# Revit family: Gira_104000
name_source: partatom
category: Elektroinstallationen
revit_build: Autodesk Revit 2017 (Build: 20160225_1515(x64)
units: mm (PartAtom-declared; Revit-internal decimal feet)

## family parameters
Basisbauteil = Fläche
Beim Laden mit Abzugskörper schneiden = Nein
Bemaßung runder Anschluss = Durchmesser verwenden
Beschriftungsausrichtung beibehalten = Nein
Gemeinsam genutzt = Nein
Raumberechnungspunkt = Nein
Teiletyp = Normal

## types (1)
- Schaltaktor 2f 16 A Hand KNX REG
    Andere Bussysteme = ohne
    Anzahl der Ausgänge = 0
    Anzahl der binären Eingänge = 0
    BIM = https://media.stage.bim.site 8f.rfa
    BIMSITE_PRODUCT_ID = 39b9523d5bf61837385f41dbcf1c51630087c11a
    Beschreibung = KNX Schaltaktor 2fach 16 A mit Handbetätigung  REG plus REG-Schaltaktoren mit integrierter Busankopplung. Zum Schalten von unabhängig ansteuerbaren Lastgruppen. Mit Handschalter zur Umschaltung des Relais (Ein Aus) parallel bzw. ohne KNX Betrieb. Anschluss mehrphasig. Keine zusätzliche Spannungsversorgung erforderlich.  Merkmale:  Handbetätigung der Relais unabhängig vom Bus bzw. der Schaltstellungsanzeige.  Schließer- oder Öffnerbetrieb.  Zentrale Schaltfunktion.  Sammelrückmeldung zur Reduzierung der Buslast.  Aktive oder passive (Objekt auslesbar) zyklische Rückmeldefunktion.  Rückmeldungen lassen sich nach Busspannungswiederkehr verzögern.  Logische Verknüpfungsfunktion für jeden Ausgang.  Sperrfunktion für jeden Kanal parametrierbar. Alternativ Zwangsstellungsfunktion für jeden Ausgang.  Zeitfunktionen (Ein- bzw. Ausschaltverzögerung, Treppenlichtfunktion - auch mit Vorwarnfunktion).  Einbeziehung in Lichtszenen möglich, max. acht interne Szenen je Kanal sind parametrierbar.  Speicherfunktion für Lichtszenen.  Betriebsstundenzähler als Vorwärts- Rückwärtszähler mit Grenzwertfunktion (Grenzwert über Bus veränderbar) für jeden Ausgang aktivierbar.  Eingangsüberwachung auf zyklische Aktualisierung mit Sicherheitsstellung.  Reaktionen bei Busspannungsausfall und -wiederkehr und nach einem ETS-Programmiervorgang für jeden Kanal einstellbar.  Unabhängiges Schalten der zwei Ausgänge.  Hinweise :  Montage auf DIN-Hutschiene.  VDE-Zulassung gemäß EN 60669-1, EN 60669-2-1.
    Blindleistung = Nein
    Breite in Teilungseinheiten = 4
    Busspannung pufferbar = Nein
    Bussystem Funkbus = Nein
    Bussystem KNX = Ja
    Bussystem KNX-Funk = Nein
    Bussystem LON = Nein
    Bussystem Powernet = Nein
    Datenblatt = https://media.stage.bim.site
    Datenblatt 1 = https://media.stage.bim.site
    GTIN = 4010337058359
    Geeignet für C-Last = Nein
    HAN = 104000
    Handschaltung = Nein
    HeinzeBIM = https://www.heinze.de
    Hersteller = Gira
    Kosten = 0 $
    Max. Anzahl der Schaltausgänge = 0
    Mit Busankopplung = Ja
    Mit LED-Anzeige = Nein
    Modulare Erweiterungsmöglichkeit = Nein
    Montageart = REG
    Produktseite = https://media.stage.bim.site
    Stellgröße schaltend = Nein
    Stellgröße stetig = Nein
    Tarifumschaltung = Nein
    Typname = Schaltaktor 2f 16 A Hand KNX REG
    URL = https://www.gira.de
    Ventilschutzfunktion = Nein
    Verschiedene Phasen anschließbar = Nein
    Vor Ort-/Handbedienung = Ja
    Vorgabe-Ansicht = 1219 mm
    Zulassung nach PTB = Nein

## geometry (parser evidence)
native form markers: Sweep x3
no freeform markers — native parametric forms only
